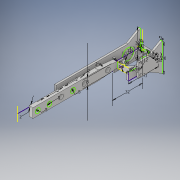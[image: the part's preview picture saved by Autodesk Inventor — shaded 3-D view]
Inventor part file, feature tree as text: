
AUTODESK INVENTOR PART (.ipt)
format: ipt  version: 2019 (Build 230136000, 136)  size: 523,776 bytes
history: native  units: in
note: dims shown in document units (in); Inventor stores cm internally (conversion verified against a paired STEP export)
features: extrude x31, sketch x28
ambient origin geometry x8: Origin, YZ Plane, XZ Plane, XY Plane, X Axis, Y Axis, Z Axis, Center Point
bodies: Solid1 (feature_tree)
feature tree (59):
  sketch  "Sketch1"  dims[d3=0.3346in d4=0.0394in]
  extrude  "Extrusion1"  Depth=0.0394in
  extrude  "Extrusion2"  Depth=0.0787in
  extrude  "Extrusion3"  Depth=0.0394in
  extrude  "Extrusion4"  Depth=0.0787in
  sketch  "Sketch3"  dims[d7=0.0787in d8=0.0394in]
  sketch  "Sketch4"  dims[d9=0.0394in d10=0.0787in]
  extrude  "Extrusion5"  Depth=0.0787in
  sketch  "Sketch5"  dims[d11=0.0787in d12=0.0787in]
  extrude  "Extrusion6"  Depth=0.0787in
  extrude  "Extrusion7"  Depth=0.0787in
  sketch  "Sketch7"  dims[d15=0.0787in d16=0.0787in]
  extrude  "Extrusion8"  Depth=0.9843in TaperAngle=0.0deg
  extrude  "Extrusion9"  Depth=0.2362in TaperAngle=0.0deg
  sketch  "Sketch10"  dims[d17=0.0787in d18=0.9843in d19=0.0in]
  extrude  "Extrusion12"  Depth=0.0787in TaperAngle=0.0deg
  extrude  "Extrusion13"  Depth=0.4724in
  sketch  "Sketch11"  dims[d20=0.1181in d21=0.0in d22=0.2362in d23=0.0in]
  extrude  "Extrusion14"  TaperAngle=45.0deg  [1 undecoded]
  sketch  "Sketch13"  dims[d28=0.1181in d29=0.0in d30=0.4724in]
  extrude  "Extrusion21"  Depth=0.4724in
  extrude  "Extrusion22"  TaperAngle=45.0deg  [1 undecoded]
  extrude  "Extrusion23"  Depth=0.0787in
  extrude  "Extrusion24"  Depth=0.3937in TaperAngle=0.0deg
  extrude  "Extrusion25"  Depth=0.0787in
  extrude  "Extrusion26"  Depth=0.0787in
  sketch  "Sketch24"  dims[d63=0.2362in d64=0.0787in]
  sketch  "Sketch25"  dims[d65=0.2362in d66=0.0787in]
  extrude  "Extrusion27"  Depth=0.0787in
  extrude  "Extrusion28"  Depth=0.0787in
  sketch  "Sketch26"  dims[d67=1.1811in d68=0.0787in]
  extrude  "Extrusion29"  Depth=0.9843in TaperAngle=0.0deg
  extrude  "Extrusion30"  TaperAngle=30.0deg  [1 undecoded]
  extrude  "Extrusion31"  Depth=5.1181in TaperAngle=0.0deg
  extrude  "Extrusion32"  Depth=0.0787in
  extrude  "Extrusion33"  Depth=0.0787in
  extrude  "Extrusion34"  Depth=1.9685in
  sketch  "Sketch31"  dims[d81=0.0787in d82=0.0787in]
  extrude  "Extrusion35"  Depth=0.1575in TaperAngle=0.0deg
  extrude  "Extrusion36"  Depth=0.1969in
  extrude  "Extrusion37"  Depth=0.9843in
  sketch  "Sketch32"  dims[d83=0.0787in d106=1.9685in]
  extrude  "Extrusion38"  Depth=0.1969in
  sketch  "Sketch33"  dims[d107=0.3937in d108=0.1575in d109=0.0in]
  extrude  "Extrusion39"  Depth=0.9843in
  sketch  "Sketch2"  dims[d5=0.6693in d6=0.0787in]
  sketch  "Sketch6"  dims[d13=0.0787in d14=0.0787in]
  sketch  "Sketch12"  dims[d25=0.0512in d26=0.0787in d27=0.0in]
  sketch  "Sketch18"  dims[d31=45.0deg d32=45.0deg]
  sketch  "Sketch19"  dims[d33=0.0787in d34=0.0in d35=0.4724in]
  sketch  "Sketch20"  dims[d36=90.0deg d37=45.0deg]
  sketch  "Sketch21"  dims[d38=0.0787in d39=0.0in d40=0.0709in]
  sketch  "Sketch22"  dims[d41=0.1575in d42=0.3937in d43=0.0in]
  sketch  "Sketch23"  dims[d44=2.3622in d45=0.0in d62=0.0787in]
  sketch  "Sketch27"  dims[d69=1.1811in d70=0.9843in d71=0.0in]
  sketch  "Sketch28"  dims[d72=5.1181in d73=0.0in d74=30.0deg]
  sketch  "Sketch29"  dims[d75=30.0deg d76=5.1181in d77=0.0in]
  sketch  "Sketch30"  dims[d79=0.0787in d80=0.0787in]
  sketch  "Sketch34"  dims[d110=0.1575in d111=0.0in d112=0.1969in d113=0.9843in d114=0.1969in d115=0.9843in d116=0.1969in d117=0.1575in d118=0.0in d131=0.0787in d132=0.0787in d133=0.0787in d134=0.0787in d135=0.0787in d136=0.0787in d137=0.0787in d138=0.0787in d139=0.0787in d140=0.0787in d141=0.0787in d142=0.0787in d143=0.0787in d144=0.0787in d145=0.0787in d146=0.0787in d147=0.0787in d148=0.0in d149=0.0787in d150=0.0787in d151=0.0787in d152=0.0787in d153=0.0787in d154=0.0787in d155=0.0787in d156=0.0787in d157=0.0787in d158=0.0in d159=1.5748in d160=0.5906in d161=0.1969in d162=0.0in d163=1.2598in d164=0.315in d165=0.4724in d166=0.0787in d167=0.0in d168=0.0787in d169=0.0in d170=1.2598in d171=0.4724in d172=0.0787in d173=0.0in d174=0.0787in d175=0.0in d176=0.6299in d177=0.6693in d178=0.0in d179=0.6693in d180=0.0in d181=0.0394in d182=0.0394in d183=0.1575in d184=0.0in d185=0.7874in d186=0.0in d187=0.1969in d188=0.1969in d189=0.1969in d190=0.7874in d191=0.0in d192=0.7874in d193=0.0in d194=0.7874in d195=0.0in d196=0.4724in d197=0.0in d198=0.0512in d199=0.0394in d200=0.0in]
note: 3 required parameter values undecoded (feature->parameter linkage not recoverable at this tier; creation-order binding heuristic only, values carry confidence <= 0.55)
